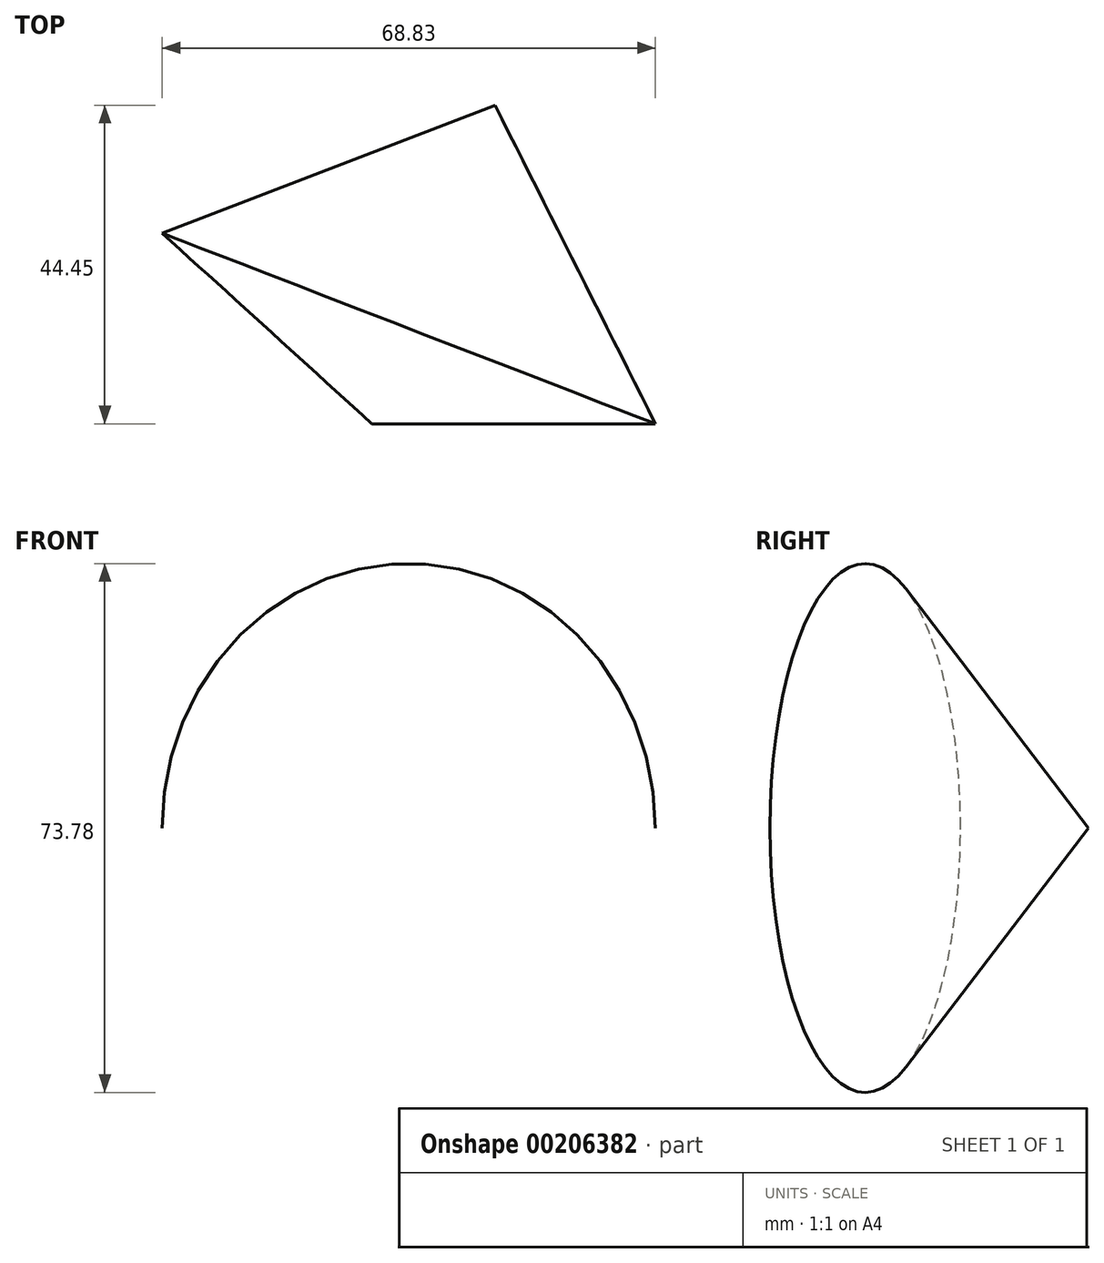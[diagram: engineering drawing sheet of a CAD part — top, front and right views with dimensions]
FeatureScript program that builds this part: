
annotation { "Feature Type Name" : "Feature", "Feature Type Description" : "" }
export const myFeature = defineFeature(function(context is Context, id is Id, definition is map)
    precondition{}
    {
        {
            var Q0;
            Q0=qCreatedBy(makeId("Top.planeOp"),FACE);
            var sketch = newSketch(context, id + "F0", { "sketchPlane" : qUnion([Q0])});
            skLineSegment(sketch, "E0", {"start": v(-7.97, 26.67) * mm, "end": v(-25.14, -17.78) * mm});
            skLineSegment(sketch, "E1", {"start": v(-25.14, -17.78) * mm, "end": v(14.4, -17.78) * mm});
            skLineSegment(sketch, "E2", {"start": v(-7.97, 26.67) * mm, "end": v(14.4, -17.78) * mm});
            skSolve(sketch);
        }
        {
            var Q0;
            Q0=makeQuery(id+"F0.imprint","IMPRINT",FACE,{"disambiguationData":[TD([[makeQuery(id+"F0.imprint","IMPRINT",EDGE,{"derivedFrom":sQuery(id+"F0.wireOp",EDGE,"E0")}),1.0]])]});
            var Q1;
            Q1=sQuery(id+"F0.wireOp",EDGE,"E0");
            revolve(context, id + "F1", {"entities" : qUnion([Q0]), "axis" : qUnion([Q1]), "revolveType" : RevolveType.FULL});
        }
    });
